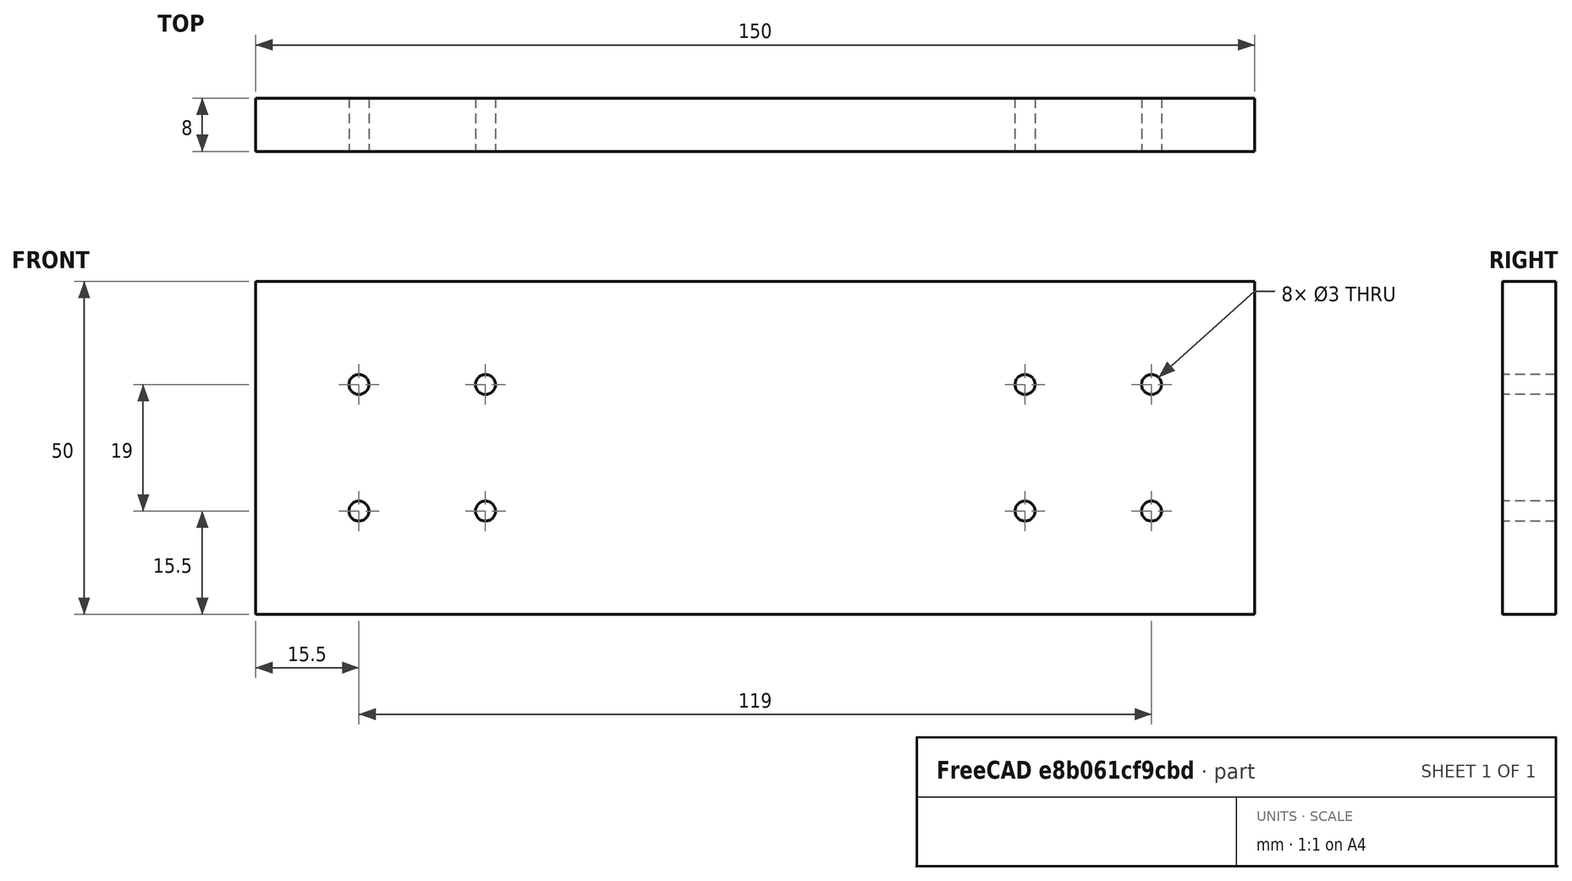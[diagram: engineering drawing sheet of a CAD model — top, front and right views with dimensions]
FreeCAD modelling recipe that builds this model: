
FCSTD DOCUMENT  (FreeCAD 0.14R3703 (Git))
Label: pletina_z_taladro_rail
License: CC-BY 3.0
LicenseURL: http://creativecommons.org/licenses/by/3.0/
objects: Part::Cylinder×8, Part::Cut×8, Part::Feature×2
note: 18 computed .brp shape members not serialized (recipe doc carries the construction recipe); baked Part::Feature solids carry a one-line shape summary decoded from their .brp

FEATURE [Part::Feature] Box  label="pletina_z_sin_agujeros"
  Placement = pos=(120,247,613) rot=(0,0,1;0rad)
  shape: bbox 150 x 8 x 50 mm, 6 faces (baked)
FEATURE [Part::Cylinder] Cylinder  label="Cilindro"
  Angle = 360
  Height = 30
  Placement = pos=(135.5,271.844,647.5) rot=(1,0,0;1.5708rad)
  Radius = 1.5
FEATURE [Part::Cylinder] Cylinder001  label="Cilindro002"
  Angle = 360
  Height = 30
  Placement = pos=(135.5,272.844,628.5) rot=(1,0,0;1.5708rad)
  Radius = 1.5
FEATURE [Part::Cylinder] Cylinder002  label="Cilindro001"
  Angle = 360
  Height = 30
  Placement = pos=(154.5,273.844,647.5) rot=(1,0,0;1.5708rad)
  Radius = 1.5
FEATURE [Part::Cylinder] Cylinder003  label="Cilindro003"
  Angle = 360
  Height = 30
  Placement = pos=(154.5,273.844,628.5) rot=(1,0,0;1.5708rad)
  Radius = 1.5
FEATURE [Part::Cylinder] Cylinder004  label="Cilindro004"
  Angle = 360
  Height = 30
  Placement = pos=(235.5,273.844,647.5) rot=(1,0,0;1.5708rad)
  Radius = 1.5
FEATURE [Part::Cylinder] Cylinder005  label="Cilindro005"
  Angle = 360
  Height = 30
  Placement = pos=(254.5,272.844,647.5) rot=(1,0,0;1.5708rad)
  Radius = 1.5
FEATURE [Part::Cylinder] Cylinder006  label="Cilindro006"
  Angle = 360
  Height = 30
  Placement = pos=(235.5,270.844,628.5) rot=(1,0,0;1.5708rad)
  Radius = 1.5
FEATURE [Part::Cylinder] Cylinder007  label="Cilindro007"
  Angle = 360
  Height = 30
  Placement = pos=(254.5,273.844,628.5) rot=(1,0,0;1.5708rad)
  Radius = 1.5
FEATURE [Part::Cut] Cut
  Base = -> Box
  Tool = -> Cylinder
FEATURE [Part::Cut] Cut001
  Base = -> Cut
  Tool = -> Cylinder007
FEATURE [Part::Cut] Cut002
  Base = -> Cut001
  Tool = -> Cylinder006
FEATURE [Part::Cut] Cut003
  Base = -> Cut002
  Tool = -> Cylinder005
FEATURE [Part::Cut] Cut004
  Base = -> Cut003
  Tool = -> Cylinder004
FEATURE [Part::Cut] Cut005
  Base = -> Cut004
  Tool = -> Cylinder003
FEATURE [Part::Cut] Cut006
  Base = -> Cut005
  Tool = -> Cylinder002
FEATURE [Part::Cut] Cut007
  Base = -> Cut006
  Tool = -> Cylinder001
FEATURE [Part::Feature] Cut008  label="pletina_z_taladro_patines"
  shape: bbox 150 x 8 x 50 mm, 14 faces (baked)
